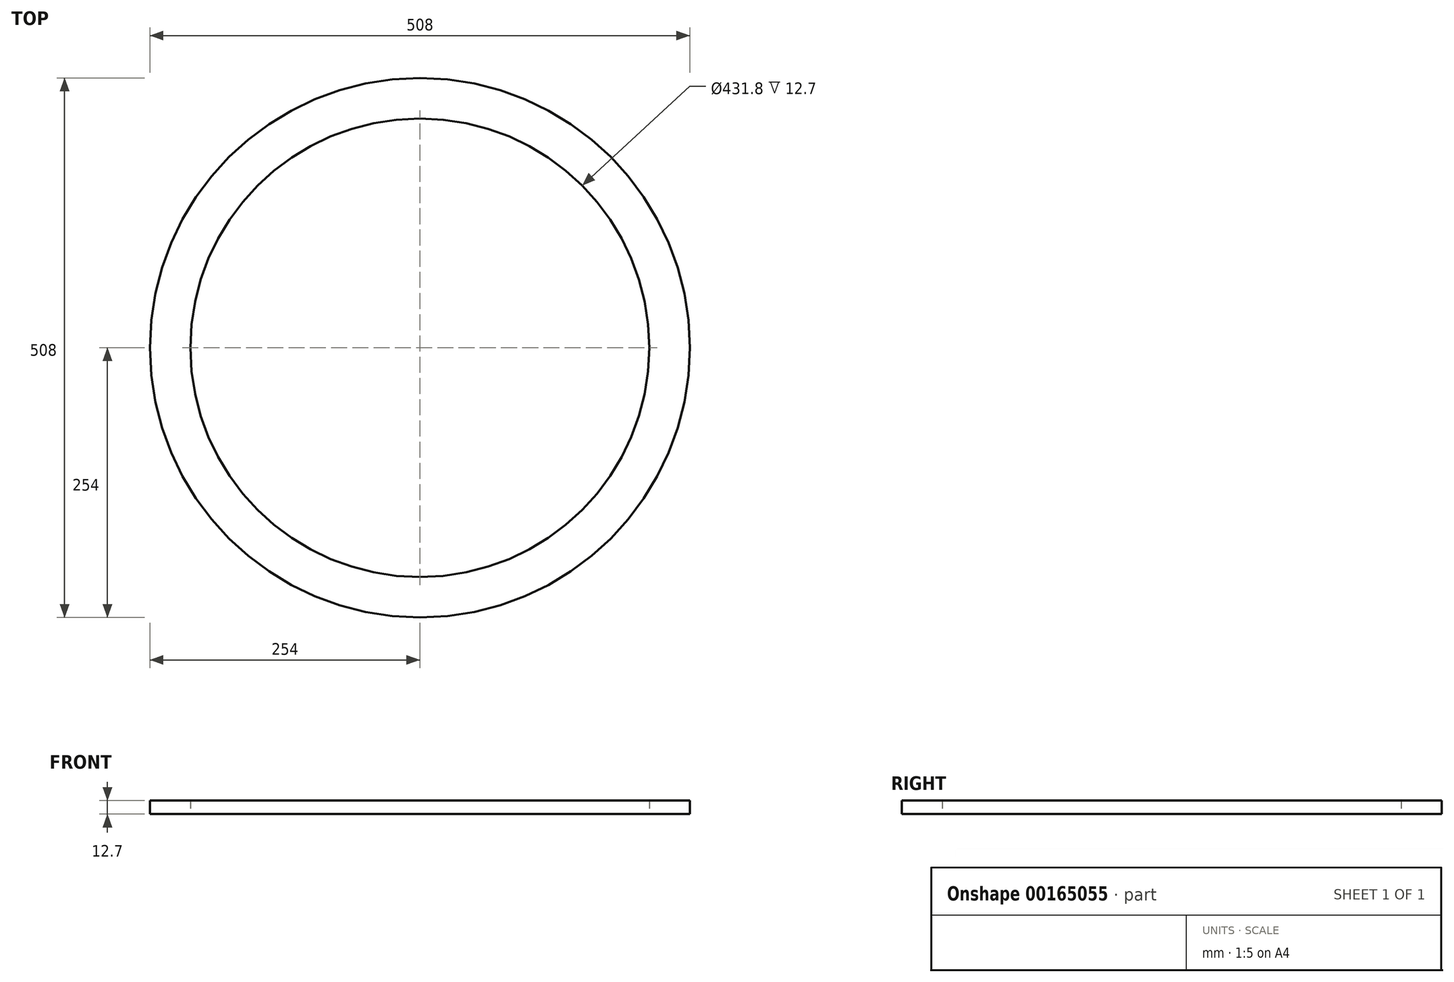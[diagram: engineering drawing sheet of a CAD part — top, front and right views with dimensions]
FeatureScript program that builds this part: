
annotation { "Feature Type Name" : "Feature", "Feature Type Description" : "" }
export const myFeature = defineFeature(function(context is Context, id is Id, definition is map)
    precondition{}
    {
        {
            var Q0;
            Q0=qCreatedBy(makeId("Top.planeOp"),FACE);
            var sketch = newSketch(context, id + "F0", { "sketchPlane" : qUnion([Q0])});
            skCircle(sketch, "E0", {"center": v(0, 0) * mm, "radius": 215.9 * mm});
            skCircle(sketch, "E1", {"center": v(0, 0) * mm, "radius": 254 * mm});
            skSolve(sketch);
        }
        {
            var Q0;
            Q0 = qSketchRegion(id + "F0", true);
            extrude(context, id + "F1", {"entities" : qUnion([Q0]), "depth" : 12.7 * mm});
        }
    });
